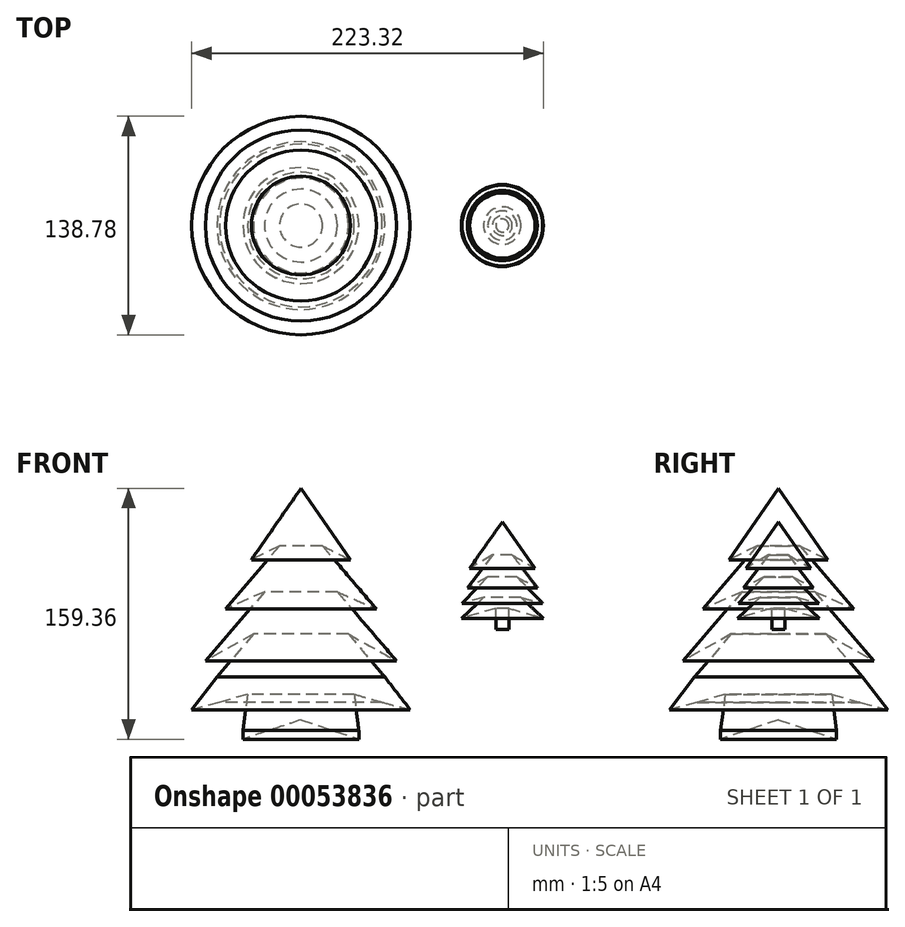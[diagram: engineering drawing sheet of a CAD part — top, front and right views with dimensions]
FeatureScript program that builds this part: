
annotation { "Feature Type Name" : "Feature", "Feature Type Description" : "" }
export const myFeature = defineFeature(function(context is Context, id is Id, definition is map)
    precondition{}
    {
        {
            var Q0;
            Q0=qCreatedBy(makeId("Front.planeOp"),FACE);
            var sketch = newSketch(context, id + "F0", { "sketchPlane" : qUnion([Q0])});
            skLineSegment(sketch, "E0", {"start": v(-117.71, -84.58) * mm, "end": v(-114.82, -61.44) * mm});
            skLineSegment(sketch, "E1", {"start": v(-132.58, -66.56) * mm, "end": v(-114.82, -61.44) * mm});
            skLineSegment(sketch, "E2", {"start": v(-150.34, -71.28) * mm, "end": v(-132.58, -66.56) * mm});
            skLineSegment(sketch, "E3", {"start": v(-134.23, -50.52) * mm, "end": v(-150.34, -71.28) * mm});
            skLineSegment(sketch, "E4", {"start": v(-134.23, -50.52) * mm, "end": v(-111.1, -23.2) * mm});
            skLineSegment(sketch, "E5", {"start": v(-111.1, -23.2) * mm, "end": v(-141.67, -40.28) * mm});
            skLineSegment(sketch, "E6", {"start": v(-141.67, -40.28) * mm, "end": v(-104.08, 3.62) * mm});
            skLineSegment(sketch, "E7", {"start": v(-104.08, 3.62) * mm, "end": v(-128.86, -7.26) * mm});
            skLineSegment(sketch, "E8", {"start": v(-128.86, -7.26) * mm, "end": v(-94.58, 32.8) * mm});
            skLineSegment(sketch, "E9", {"start": v(-94.58, 32.8) * mm, "end": v(-112.34, 23.95) * mm});
            skLineSegment(sketch, "E10", {"start": v(-112.34, 23.95) * mm, "end": v(-80.95, 69.35) * mm});
            skLineSegment(sketch, "E11", {"start": v(-80.95, 69.35) * mm, "end": v(-80.95, -77.69) * mm});
            skLineSegment(sketch, "E12", {"start": v(-80.95, -77.69) * mm, "end": v(-117.71, -90) * mm});
            skLineSegment(sketch, "E13", {"start": v(-117.71, -90) * mm, "end": v(-117.71, -84.58) * mm});
            skSolve(sketch);
        }
        {
            var Q0;
            Q0 = qSketchRegion(id + "F0", true);
            var Q1;
            Q1=sQuery(id+"F0.wireOp",EDGE,"E11");
            revolve(context, id + "F1", {"entities" : qUnion([Q0]), "axis" : qUnion([Q1]), "revolveType" : RevolveType.FULL});
        }
        {
            var Q0;
            Q0=qCreatedBy(makeId("Front.planeOp"),FACE);
            var sketch = newSketch(context, id + "F2", { "sketchPlane" : qUnion([Q0])});
            skLineSegment(sketch, "E14", {"start": v(51.1, -20.25) * mm, "end": v(51.1, -6.94) * mm});
            skLineSegment(sketch, "E15", {"start": v(51.1, -6.94) * mm, "end": v(72.98, -13.15) * mm});
            skLineSegment(sketch, "E16", {"start": v(72.98, -13.15) * mm, "end": v(58.84, 0) * mm});
            skLineSegment(sketch, "E17", {"start": v(58.84, 0) * mm, "end": v(72.54, -3.66) * mm});
            skLineSegment(sketch, "E18", {"start": v(72.54, -3.66) * mm, "end": v(56.23, 13.09) * mm});
            skLineSegment(sketch, "E19", {"start": v(56.23, 13.09) * mm, "end": v(69.23, 6.08) * mm});
            skLineSegment(sketch, "E20", {"start": v(69.23, 6.08) * mm, "end": v(53.24, 27.02) * mm});
            skLineSegment(sketch, "E21", {"start": v(53.24, 27.02) * mm, "end": v(67.7, 18.56) * mm});
            skLineSegment(sketch, "E22", {"start": v(67.7, 18.56) * mm, "end": v(46.96, 48.04) * mm});
            skLineSegment(sketch, "E23", {"start": v(46.96, 48.04) * mm, "end": v(46.96, -20.15) * mm});
            skLineSegment(sketch, "E24", {"start": v(46.96, -20.15) * mm, "end": v(51.1, -20.25) * mm});
            skSolve(sketch);
        }
        {
            var Q0;
            Q0 = qSketchRegion(id + "F2", true);
            var Q1;
            Q1=sQuery(id+"F2.wireOp",EDGE,"E23");
            revolve(context, id + "F3", {"entities" : qUnion([Q0]), "axis" : qUnion([Q1]), "revolveType" : RevolveType.FULL});
        }
    });
